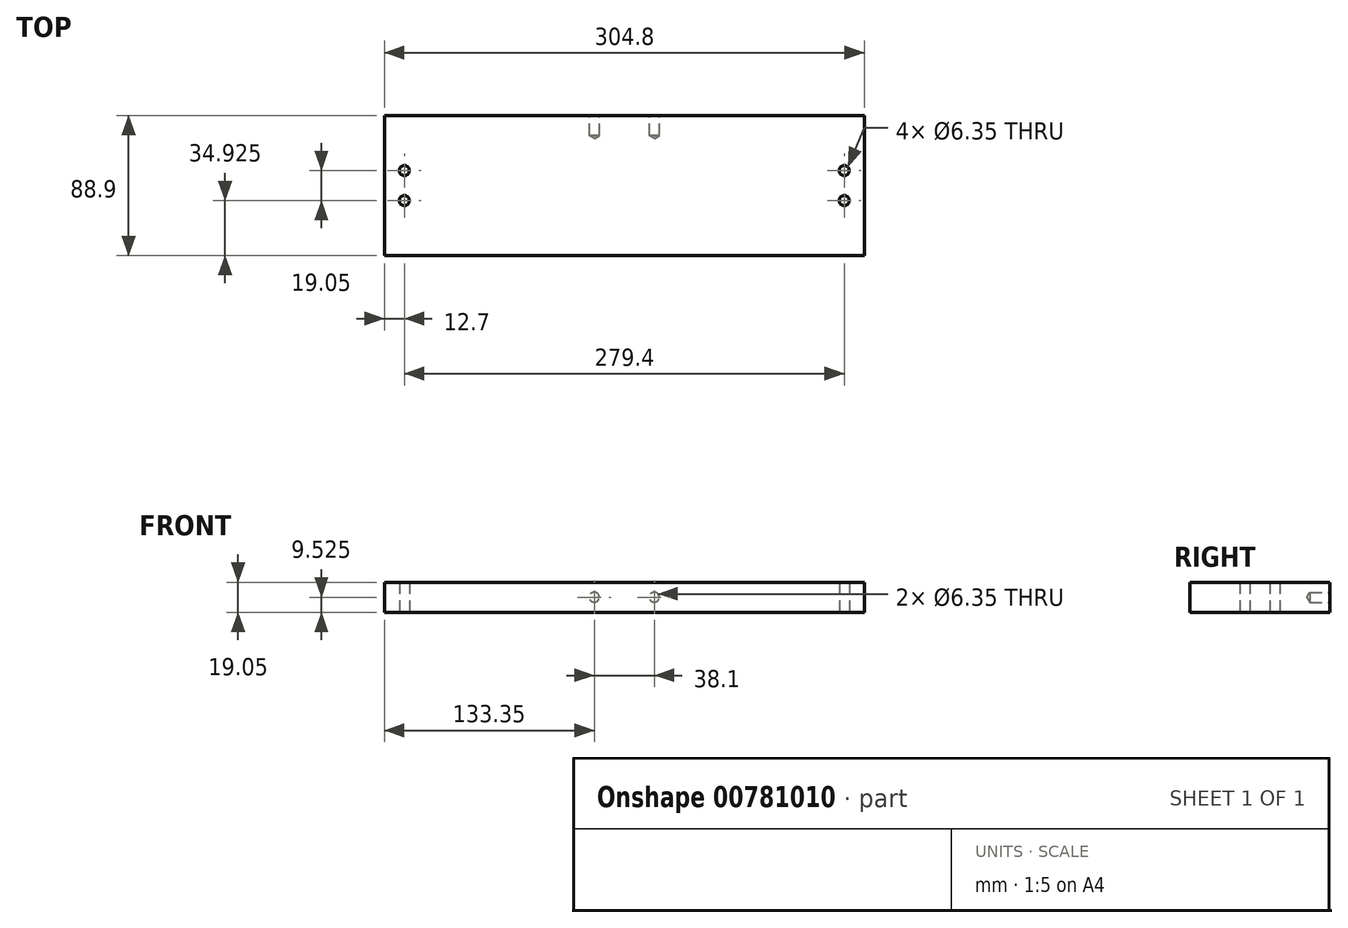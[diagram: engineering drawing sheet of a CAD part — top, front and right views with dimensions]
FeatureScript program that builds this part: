
annotation { "Feature Type Name" : "Feature", "Feature Type Description" : "" }
export const myFeature = defineFeature(function(context is Context, id is Id, definition is map)
    precondition{}
    {
        {
            var Q0;
            Q0=qCreatedBy(makeId("Top.planeOp"),FACE);
            var sketch = newSketch(context, id + "F0", { "sketchPlane" : qUnion([Q0])});
            skLineSegment(sketch, "E0.bottom", {"start": v(0, 0) * mm, "end": v(-152.4, 0) * mm});
            skLineSegment(sketch, "E0.top", {"start": v(0, 88.9) * mm, "end": v(-152.4, 88.9) * mm});
            skLineSegment(sketch, "E0.left", {"start": v(0, 0) * mm, "end": v(0, 88.9) * mm});
            skLineSegment(sketch, "E0.right", {"start": v(-152.4, 0) * mm, "end": v(-152.4, 88.9) * mm});
            skSolve(sketch);
        }
        {
            var Q0;
            Q0=makeQuery(id+"F0.imprint","IMPRINT",FACE,{"disambiguationData":[TD([[makeQuery(id+"F0.imprint","IMPRINT",EDGE,{"derivedFrom":sQuery(id+"F0.wireOp",EDGE,"E0.bottom")}),-1.0]])]});
            extrude(context, id + "F1", {"entities" : qUnion([Q0]), "depth" : 19.05 * mm, "offsetDistance" : 25.4 * mm});
        }
        {
            var Q0;
            Q0=makeQuery(id+"F1.opExtrude","SWEPT_BODY",BODY,{"disambiguationData":[OSD([sQuery(id+"F0.wireOp",EDGE,"E0.bottom"),sQuery(id+"F0.wireOp",EDGE,"E0.top"),sQuery(id+"F0.wireOp",EDGE,"E0.left"),sQuery(id+"F0.wireOp",EDGE,"E0.right")])]});
            var Q1;
            Q1=makeQuery(id+"F1.opExtrude","SWEPT_FACE",FACE,{"disambiguationData":[OSD([sQuery(id+"F0.wireOp",EDGE,"E0.right")])]});
            mirror(context, id + "F2", {"operationType" : NewBodyOperationType.ADD, "entities" : qUnion([Q0]), "mirrorPlane" : qUnion([Q1])});
        }
        {
            var Q0;
            {var subQ0=makeQuery(id+"F1.opExtrude","SWEPT_FACE",FACE,{"disambiguationData":[OSD([sQuery(id+"F0.wireOp",EDGE,"E0.top")])]});Q0=makeQuery(id+"F2.boolean.opBoolean","MERGE",FACE,{"derivedFrom":[subQ0,makeQuery(id+"F2.opPattern","COPY",FACE,{"derivedFrom":subQ0,"instanceName":"1"})]});}
            var sketch = newSketch(context, id + "F3", { "sketchPlane" : qUnion([Q0])});
            skLineSegment(sketch, "E1", {"start": v(2.54, 9.53) * mm, "end": v(302.26, 9.53) * mm, "construction": true});
            skLineSegment(sketch, "E2", {"start": v(133.35, 0) * mm, "end": v(133.35, 19.05) * mm, "construction": true});
            skLineSegment(sketch, "E3", {"start": v(171.45, 19.05) * mm, "end": v(171.45, 0) * mm, "construction": true});
            skPoint(sketch, "E4", {"position": v(133.35, 9.53) * mm});
            skPoint(sketch, "E5", {"position": v(171.45, 9.53) * mm});
            skSolve(sketch);
        }
        {
            var Q0;
            Q0=sQuery(id+"F3.wireOp",VERTEX,"E4");
            var Q1;
            Q1=sQuery(id+"F3.wireOp",VERTEX,"E5");
            var Q2;
            Q2=makeQuery(id+"F1.opExtrude","SWEPT_BODY",BODY,{"disambiguationData":[OSD([sQuery(id+"F0.wireOp",EDGE,"E0.bottom"),sQuery(id+"F0.wireOp",EDGE,"E0.top"),sQuery(id+"F0.wireOp",EDGE,"E0.left"),sQuery(id+"F0.wireOp",EDGE,"E0.right")])]});
            hole(context, id + "F4", {"style" : HoleStyle.SIMPLE, "endStyle" : HoleEndStyle.BLIND, "holeDiameter" : 6.35 * mm, "majorDiameter" : 6.35 * mm, "holeDepth" : 12.7 * mm, "isTappedThrough" : true, "tappedDepth" : 12.7 * mm, "tapClearance" : 3, "locations" : qUnion([Q0, Q1]), "scope" : qUnion([Q2])});
        }
        {
            var Q0;
            {var subQ0=makeQuery(id+"F1.opExtrude","CAP_FACE",FACE,{"disambiguationData":[OSD([sQuery(id+"F0.wireOp",EDGE,"E0.bottom"),sQuery(id+"F0.wireOp",EDGE,"E0.top"),sQuery(id+"F0.wireOp",EDGE,"E0.left"),sQuery(id+"F0.wireOp",EDGE,"E0.right")])],"isStart":true});Q0=makeQuery(id+"F2.boolean.opBoolean","MERGE",FACE,{"derivedFrom":[subQ0,makeQuery(id+"F2.opPattern","COPY",FACE,{"derivedFrom":subQ0,"instanceName":"1"})]});}
            var sketch = newSketch(context, id + "F5", { "sketchPlane" : qUnion([Q0])});
            skLineSegment(sketch, "E6", {"start": v(-292.1, 0) * mm, "end": v(-292.1, -88.9) * mm, "construction": true});
            skPoint(sketch, "E7", {"position": v(-292.1, -34.93) * mm});
            skPoint(sketch, "E8", {"position": v(-292.1, -53.98) * mm});
            skLineSegment(sketch, "E9", {"start": v(-152.4, -88.9) * mm, "end": v(-152.4, 0) * mm, "construction": true});
            skPoint(sketch, "E10.MirrorP", {"position": v(-12.7, -34.92) * mm});
            skPoint(sketch, "E11.MirrorP", {"position": v(-12.7, -53.97) * mm});
            skSolve(sketch);
        }
        {
            var Q0;
            Q0=sQuery(id+"F5.wireOp",VERTEX,"E10.MirrorP");
            var Q1;
            Q1=sQuery(id+"F5.wireOp",VERTEX,"E11.MirrorP");
            var Q2;
            Q2=sQuery(id+"F5.wireOp",VERTEX,"E7");
            var Q3;
            Q3=sQuery(id+"F5.wireOp",VERTEX,"E8");
            var Q4;
            Q4=makeQuery(id+"F1.opExtrude","SWEPT_BODY",BODY,{"disambiguationData":[OSD([sQuery(id+"F0.wireOp",EDGE,"E0.bottom"),sQuery(id+"F0.wireOp",EDGE,"E0.top"),sQuery(id+"F0.wireOp",EDGE,"E0.left"),sQuery(id+"F0.wireOp",EDGE,"E0.right")])]});
            hole(context, id + "F6", {"style" : HoleStyle.SIMPLE, "endStyle" : HoleEndStyle.THROUGH, "holeDiameter" : 6.35 * mm, "majorDiameter" : 6.35 * mm, "isTappedThrough" : true, "tappedDepth" : 12.7 * mm, "tapClearance" : 3, "locations" : qUnion([Q0, Q1, Q2, Q3]), "scope" : qUnion([Q4])});
        }
    });
